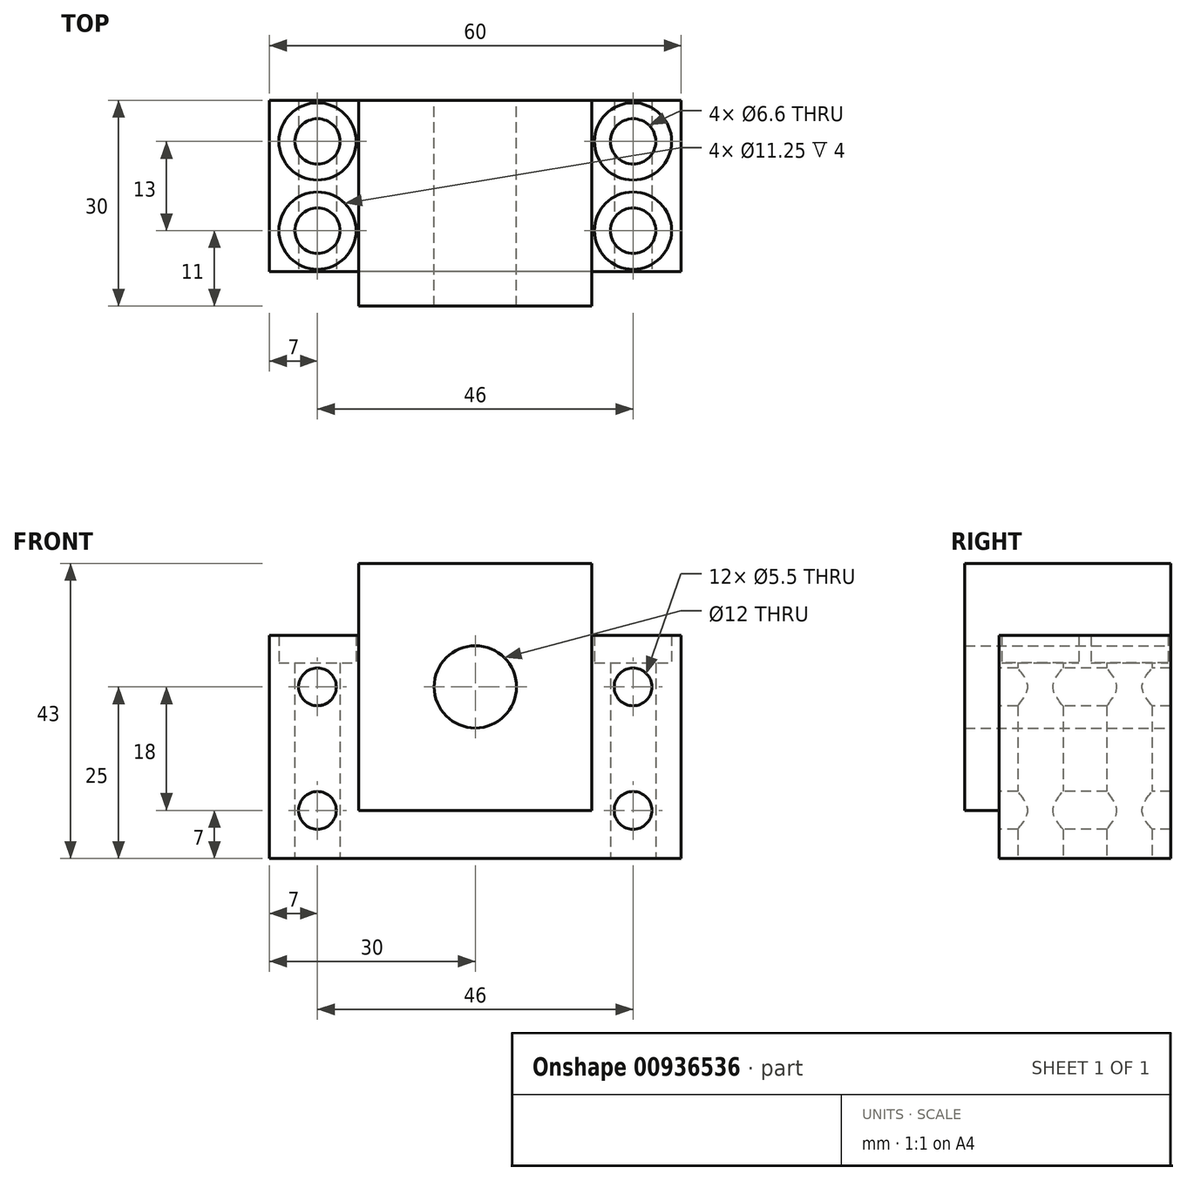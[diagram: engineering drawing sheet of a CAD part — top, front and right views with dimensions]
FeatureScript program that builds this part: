
annotation { "Feature Type Name" : "Feature", "Feature Type Description" : "" }
export const myFeature = defineFeature(function(context is Context, id is Id, definition is map)
    precondition{}
    {
        {
            var Q0;
            Q0=qCreatedBy(makeId("Front.planeOp"),FACE);
            var sketch = newSketch(context, id + "F0", { "sketchPlane" : qUnion([Q0])});
            skLineSegment(sketch, "E0.bottom", {"start": v(30, 16.25) * mm, "end": v(17, 16.25) * mm});
            skLineSegment(sketch, "E0.top", {"start": v(30, -16.25) * mm, "end": v(-30, -16.25) * mm});
            skLineSegment(sketch, "E0.left", {"start": v(30, 16.25) * mm, "end": v(30, -16.25) * mm});
            skLineSegment(sketch, "E0.right", {"start": v(-30, 16.25) * mm, "end": v(-30, -16.25) * mm});
            skPoint(sketch, "E0.middle", {"position": v(0, 0) * mm});
            skLineSegment(sketch, "E1.bottom", {"start": v(17, 26.75) * mm, "end": v(-17, 26.75) * mm});
            skLineSegment(sketch, "E1.left", {"start": v(17, 26.75) * mm, "end": v(17, 16.25) * mm});
            skLineSegment(sketch, "E1.right", {"start": v(-17, 26.75) * mm, "end": v(-17, 16.25) * mm});
            skPoint(sketch, "E1.middle", {"position": v(0, 8.75) * mm});
            skCircle(sketch, "E2", {"center": v(0, 8.75) * mm, "radius": 6 * mm});
            skLineSegment(sketch, "E3.trimOffspring", {"start": v(-17, 16.25) * mm, "end": v(-30, 16.25) * mm});
            skPoint(sketch, "E4", {"position": v(23, -9.25) * mm});
            skPoint(sketch, "E5", {"position": v(23, 8.75) * mm});
            skPoint(sketch, "E6.MirrorP", {"position": v(-23, 8.75) * mm});
            skPoint(sketch, "E7.MirrorP", {"position": v(-23, -9.25) * mm});
            skSolve(sketch);
        }
        {
            var Q0;
            Q0=makeQuery(id+"F0.imprint","IMPRINT",FACE,{"disambiguationData":[TD([[makeQuery(id+"F0.imprint","IMPRINT",EDGE,{"derivedFrom":sQuery(id+"F0.wireOp",EDGE,"E0.bottom")}),1.0]])]});
            extrude(context, id + "F1", {"entities" : qUnion([Q0]), "depth" : 25 * mm, "offsetDistance" : 25 * mm});
        }
        {
            var Q0;
            Q0=makeQuery(id+"F1.opExtrude","SWEPT_FACE",FACE,{"disambiguationData":[OSD([sQuery(id+"F0.wireOp",EDGE,"E0.bottom")])]});
            var sketch = newSketch(context, id + "F2", { "sketchPlane" : qUnion([Q0])});
            skPoint(sketch, "E8", {"position": v(23, -6) * mm});
            skPoint(sketch, "E9.MirrorP", {"position": v(-23, -6) * mm});
            skPoint(sketch, "E10", {"position": v(-23, -19) * mm});
            skPoint(sketch, "E11", {"position": v(23, -19) * mm});
            skSolve(sketch);
        }
        {
            var Q0;
            Q0=sQuery(id+"F2.wireOp",VERTEX,"E9.MirrorP");
            var Q1;
            Q1=sQuery(id+"F2.wireOp",VERTEX,"E8");
            var Q2;
            Q2=sQuery(id+"F2.wireOp",VERTEX,"E11");
            var Q3;
            Q3=sQuery(id+"F2.wireOp",VERTEX,"E10");
            var Q4;
            Q4=makeQuery(id+"F1.opExtrude","SWEPT_BODY",BODY,{"disambiguationData":[OSD([sQuery(id+"F0.wireOp",EDGE,"E0.bottom"),sQuery(id+"F0.wireOp",EDGE,"E0.top"),sQuery(id+"F0.wireOp",EDGE,"E0.left"),sQuery(id+"F0.wireOp",EDGE,"E0.right"),sQuery(id+"F0.wireOp",EDGE,"E1.bottom"),sQuery(id+"F0.wireOp",EDGE,"E1.left"),sQuery(id+"F0.wireOp",EDGE,"E1.right"),sQuery(id+"F0.wireOp",EDGE,"E2"),sQuery(id+"F0.wireOp",EDGE,"E3.trimOffspring")])]});
            hole(context, id + "F3", {"style" : HoleStyle.C_BORE, "endStyle" : HoleEndStyle.THROUGH, "holeDiameter" : 6.6 * mm, "cBoreDiameter" : 11.25 * mm, "cBoreDepth" : 4 * mm, "majorDiameter" : 5 * mm, "tappedDepth" : 12 * mm, "tapClearance" : 3, "locations" : qUnion([Q0, Q1, Q2, Q3]), "scope" : qUnion([Q4]), "startStyle" : HoleStartStyle.PART});
        }
        {
            var Q0;
            Q0=sQuery(id+"F0.wireOp",VERTEX,"E5");
            var Q1;
            Q1=sQuery(id+"F0.wireOp",VERTEX,"E4");
            var Q2;
            Q2=sQuery(id+"F0.wireOp",VERTEX,"E7.MirrorP");
            var Q3;
            Q3=sQuery(id+"F0.wireOp",VERTEX,"E6.MirrorP");
            var Q4;
            Q4=makeQuery(id+"F1.opExtrude","SWEPT_BODY",BODY,{"disambiguationData":[OSD([sQuery(id+"F0.wireOp",EDGE,"E0.bottom"),sQuery(id+"F0.wireOp",EDGE,"E0.top"),sQuery(id+"F0.wireOp",EDGE,"E0.left"),sQuery(id+"F0.wireOp",EDGE,"E0.right"),sQuery(id+"F0.wireOp",EDGE,"E1.bottom"),sQuery(id+"F0.wireOp",EDGE,"E1.left"),sQuery(id+"F0.wireOp",EDGE,"E1.right"),sQuery(id+"F0.wireOp",EDGE,"E2"),sQuery(id+"F0.wireOp",EDGE,"E3.trimOffspring")])]});
            hole(context, id + "F4", {"style" : HoleStyle.SIMPLE, "endStyle" : HoleEndStyle.THROUGH, "oppositeDirection" : true, "standardTappedOrClearance" : lookupTablePath({ "fit" : "Normal", "standard" : "ISO", "size" : "M5", "type" : "Clearance" }), "standardBlindInLast" : lookupTablePath({ "fit" : "Standard", "standard" : "ISO", "size" : "M5", "type" : "Clearance" }), "holeDiameter" : 5.5 * mm, "majorDiameter" : 5 * mm, "tappedDepth" : 12 * mm, "tapClearance" : 3, "locations" : qUnion([Q0, Q1, Q2, Q3]), "scope" : qUnion([Q4]), "startStyle" : HoleStartStyle.PART});
        }
        {
            var Q0;
            Q0=makeQuery(id+"F1.opExtrude","CAP_FACE",FACE,{"disambiguationData":[OSD([sQuery(id+"F0.wireOp",EDGE,"E0.bottom"),sQuery(id+"F0.wireOp",EDGE,"E0.top"),sQuery(id+"F0.wireOp",EDGE,"E0.left"),sQuery(id+"F0.wireOp",EDGE,"E0.right"),sQuery(id+"F0.wireOp",EDGE,"E1.bottom"),sQuery(id+"F0.wireOp",EDGE,"E1.left"),sQuery(id+"F0.wireOp",EDGE,"E1.right"),sQuery(id+"F0.wireOp",EDGE,"E2"),sQuery(id+"F0.wireOp",EDGE,"E3.trimOffspring")])],"isStart":false});
            var sketch = newSketch(context, id + "F5", { "sketchPlane" : qUnion([Q0])});
            skLineSegment(sketch, "E12.bottom", {"start": v(17, 26.75) * mm, "end": v(-17, 26.75) * mm});
            skLineSegment(sketch, "E12.top", {"start": v(17, -9.25) * mm, "end": v(-17, -9.25) * mm});
            skLineSegment(sketch, "E12.left", {"start": v(17, 26.75) * mm, "end": v(17, -9.25) * mm});
            skLineSegment(sketch, "E12.right", {"start": v(-17, 26.75) * mm, "end": v(-17, -9.25) * mm});
            skPoint(sketch, "E12.middle", {"position": v(0, 8.75) * mm});
            skCircle(sketch, "E13", {"center": v(0, 8.75) * mm, "radius": 6 * mm});
            skSolve(sketch);
        }
        {
            var Q0;
            Q0=qSketchRegion(id+"F5",true);
            extrude(context, id + "F6", {"entities" : qUnion([Q0]), "operationType" : NewBodyOperationType.ADD, "depth" : 5 * mm, "offsetDistance" : 25 * mm});
        }
    });
